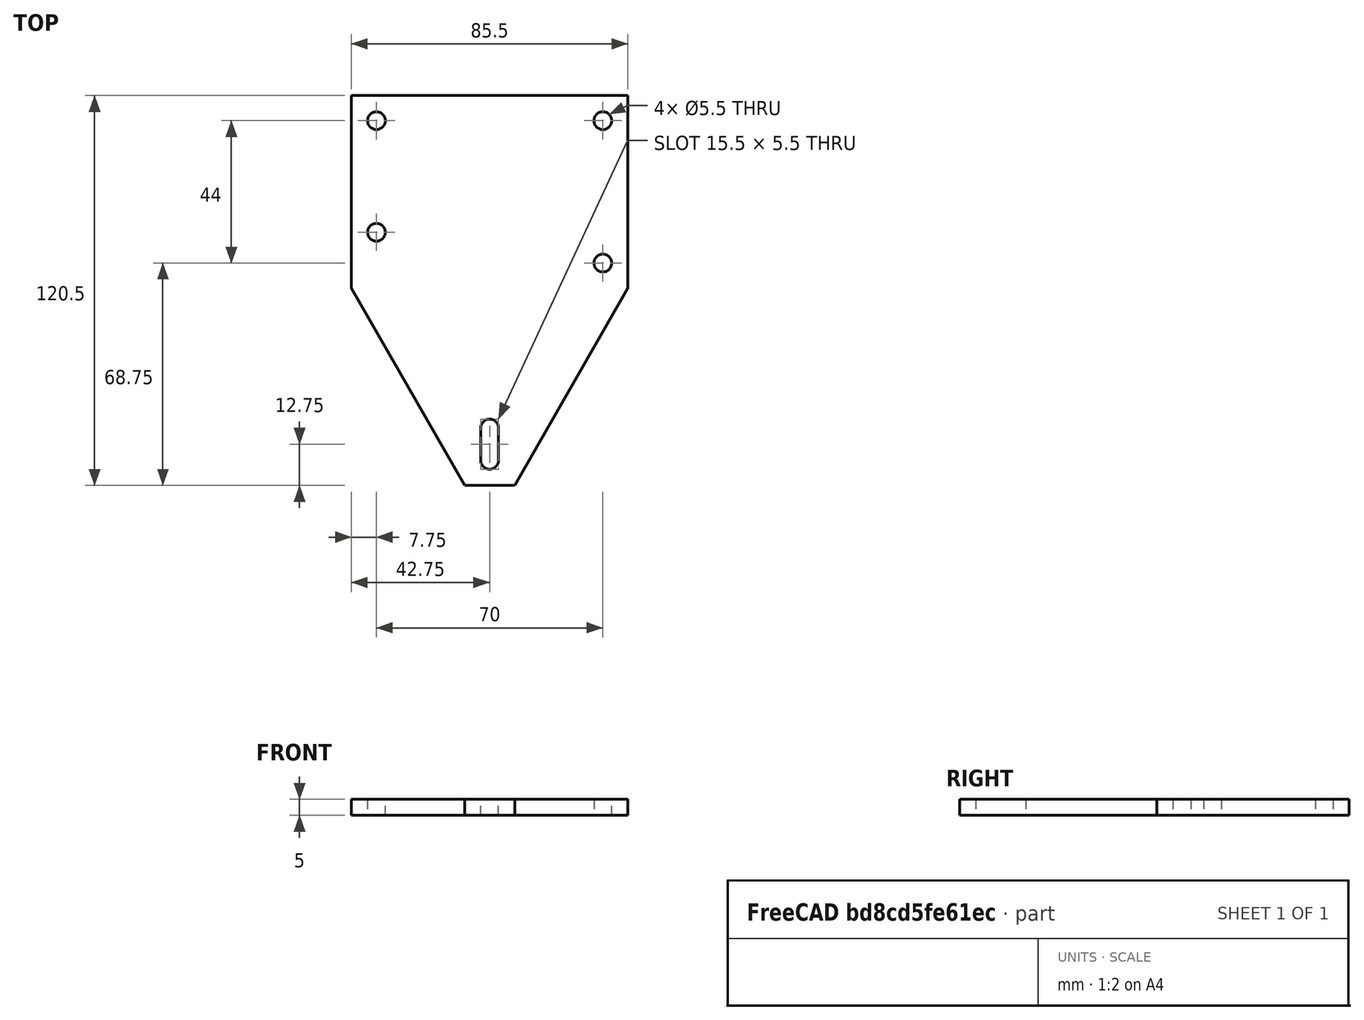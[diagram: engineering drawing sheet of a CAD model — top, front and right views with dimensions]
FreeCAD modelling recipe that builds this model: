
FCSTD DOCUMENT  (FreeCAD 0.19R)
Label: x-axis-top-carriage
License: All rights reserved
LicenseURL: http://en.wikipedia.org/wiki/All_rights_reserved
objects: Sketcher::SketchObject×1, PartDesign::Pad×1, PartDesign::Body×1
note: 4 computed .brp shape members not serialized (recipe doc carries the construction recipe); baked Part::Feature solids carry a one-line shape summary decoded from their .brp

FEATURE [Sketcher::SketchObject] Sketch
  FullyConstrained = true
  MapMode = 5
  Support = -> [XY_Plane]
  sketch-geometry (36):
    g0: LineSegment StartX=35 StartY=0 StartZ=0 EndX=50.5 EndY=0 EndZ=0
    g1: LineSegment StartX=50.5 StartY=0 StartZ=0 EndX=85.5 EndY=61 EndZ=0
    g2: LineSegment StartX=85.5 StartY=61 StartZ=0 EndX=85.5 EndY=120.5 EndZ=0
    g3: LineSegment StartX=0 StartY=120.5 StartZ=0 EndX=0 EndY=61 EndZ=0
    g4: LineSegment StartX=0 StartY=61 StartZ=0 EndX=35 EndY=0 EndZ=0
    g5: LineSegment StartX=42.75 StartY=120.5 StartZ=0 EndX=42.75 EndY=0 EndZ=0
    g6: LineSegment StartX=0 StartY=61 StartZ=0 EndX=85.5 EndY=61 EndZ=0
    g7: GeomPoint X=42.75 Y=61 Z=0
    g8: LineSegment StartX=40 StartY=17.75 StartZ=0 EndX=45.5 EndY=17.75 EndZ=0
    g9: LineSegment StartX=45.5 StartY=17.75 StartZ=0 EndX=45.5 EndY=7.75 EndZ=0
    g10: LineSegment StartX=45.5 StartY=7.75 StartZ=0 EndX=40 EndY=7.75 EndZ=0
    g11: LineSegment StartX=40 StartY=7.75 StartZ=0 EndX=40 EndY=17.75 EndZ=0
    g12: ArcOfCircle CenterX=42.75 CenterY=17.75 CenterZ=0 NormalX=0 NormalY=0 NormalZ=1 AngleXU=0 Radius=2.75 StartAngle=-2.7e-15 EndAngle=3.14159
    g13: ArcOfCircle CenterX=42.75 CenterY=7.75 CenterZ=0 NormalX=0 NormalY=0 NormalZ=1 AngleXU=0 Radius=2.75 StartAngle=3.14159 EndAngle=6.28319
    g14: GeomPoint X=42.75 Y=10.5 Z=0
    g15: GeomPoint X=42.75 Y=12.75 Z=0
    g16: LineSegment StartX=0 StartY=112.75 StartZ=0 EndX=85.5 EndY=112.75 EndZ=0
    g17: GeomPoint X=42.75 Y=112.75 Z=0
    g18: Circle CenterX=7.75 CenterY=112.75 CenterZ=0 NormalX=0 NormalY=0 NormalZ=1 AngleXU=0 Radius=2.75
    g19: Circle CenterX=77.75 CenterY=112.75 CenterZ=0 NormalX=0 NormalY=0 NormalZ=1 AngleXU=0 Radius=2.75
    g20: LineSegment StartX=7.75 StartY=120.5 StartZ=0 EndX=7.75 EndY=61 EndZ=0
    g21: GeomPoint X=7.75 Y=115.5 Z=0
    g22: GeomPoint X=5 Y=112.75 Z=0
    g23: GeomPoint X=42.75 Y=5 Z=0
    g24: LineSegment StartX=77.75 StartY=120.5 StartZ=0 EndX=77.75 EndY=61 EndZ=0
    g25: GeomPoint X=77.75 Y=115.5 Z=0
    g26: GeomPoint X=80.5 Y=112.75 Z=0
    g27: GeomPoint X=42.75 Y=62.75 Z=0
    g28: LineSegment StartX=0 StartY=68.75 StartZ=0 EndX=85.5 EndY=68.75 EndZ=0
    g29: GeomPoint X=42.75 Y=68.75 Z=0
    g30: LineSegment StartX=0 StartY=78.25 StartZ=0 EndX=85.5 EndY=78.25 EndZ=0
    g31: GeomPoint X=42.75 Y=78.25 Z=0
    g32: Circle CenterX=77.75 CenterY=68.75 CenterZ=0 NormalX=0 NormalY=0 NormalZ=1 AngleXU=0 Radius=2.75
    g33: Circle CenterX=7.75 CenterY=78.25 CenterZ=0 NormalX=0 NormalY=0 NormalZ=1 AngleXU=0 Radius=2.75
    g34: GeomPoint X=77.75 Y=66 Z=0
    g35: LineSegment StartX=0 StartY=120.5 StartZ=0 EndX=85.5 EndY=120.5 EndZ=0
  constraints (94):
    c: PointOnObject(g0,g-1)
    c: PointOnObject(g0,g-1)
    c: Coincident(g1,g0)
    c: Coincident(g2,g1)
    c: Vertical(g2)
    c: PointOnObject(g3,g-2)
    c: PointOnObject(g3,g-2)
    c: Coincident(g4,g3)
    c: Coincident(g4,g0)
    c: Vertical(g5)
    c: Symmetric(g0,g0,g5)
    c: Coincident(g6,g3)
    c: Coincident(g6,g1)
    c: Horizontal(g6)
    c: Symmetric(g1,g3,g7)
    c: Coincident(g8,g9)
    c: Coincident(g9,g10)
    c: Coincident(g10,g11)
    c: Coincident(g11,g8)
    c: Horizontal(g8)
    c: Horizontal(g10)
    c: Vertical(g9)
    c: Vertical(g11)
    c: PointOnObject(g12,g8)
    c: Coincident(g12,g8)
    c: Coincident(g12,g8)
    c: PointOnObject(g13,g10)
    c: Coincident(g13,g10)
    c: Coincident(g13,g9)
    c: PointOnObject(g13,g5)
    c: Diameter(g13) = 5.5
    c: PointOnObject(g14,g13)
    c: PointOnObject(g14,g5)
    c: DistanceX(g9,g0) = 5
    c: Symmetric(g12,g13,g15)
    c: PointOnObject(g16,g3)
    c: PointOnObject(g16,g2)
    c: Horizontal(g16)
    c: PointOnObject(g17,g5)
    c: PointOnObject(g17,g16)
    c: PointOnObject(g18,g16)
    c: PointOnObject(g19,g16)
    c: PointOnObject(g20,g6)
    c: Vertical(g20)
    c: PointOnObject(g18,g20)
    c: PointOnObject(g21,g18)
    c: PointOnObject(g21,g20)
    c: DistanceY(g21,g20) = 5
    c: PointOnObject(g22,g18)
    c: PointOnObject(g22,g16)
    c: DistanceX(g16,g22) = 5
    c: DistanceY(g15,g17) = 100
    c: PointOnObject(g23,g13)
    c: PointOnObject(g23,g5)
    c: DistanceY(g5,g23) = 5
    c: DistanceY(g9,g9) = 10
    c: Equal(g18,g19)
    c: Diameter(g18) = 5.5
    c: PointOnObject(g24,g6)
    c: Vertical(g24)
    c: PointOnObject(g19,g24)
    c: PointOnObject(g25,g19)
    c: PointOnObject(g26,g19)
    c: PointOnObject(g25,g24)
    c: PointOnObject(g26,g16)
    c: Symmetric(g17,g15,g27)
    c: PointOnObject(g28,g3)
    c: PointOnObject(g28,g2)
    c: Horizontal(g28)
    c: PointOnObject(g29,g28)
    c: PointOnObject(g29,g5)
    c: DistanceY(g27,g29) = 6
    c: PointOnObject(g30,g3)
    c: PointOnObject(g30,g2)
    c: Horizontal(g30)
    c: PointOnObject(g31,g30)
    c: PointOnObject(g31,g5)
    c: DistanceY(g27,g31) = 15.5
    c: DistanceX(g18,g19) = 70
    c: PointOnObject(g32,g28)
    c: PointOnObject(g33,g30)
    c: PointOnObject(g33,g20)
    c: PointOnObject(g32,g24)
    c: Equal(g33,g32)
    c: Equal(g32,g18)
    c: PointOnObject(g34,g32)
    c: PointOnObject(g34,g24)
    c: DistanceY(g24,g34) = 5
    c: Symmetric(g2,g3,g5)
    c: Symmetric(g24,g20,g5)
    c: Coincident(g35,g3)
    c: Coincident(g35,g2)
    c: Horizontal(g35)
    c: PointOnObject(g20,g35)
FEATURE [PartDesign::Pad] Pad
  Direction = (1,1,1)
  Length = 5
  Length2 = 100
  Profile = -> Sketch
  Type = 0
FEATURE [PartDesign::Body] Body
  Group = -> [Sketch,Pad]
  Origin = -> Origin
  Tip = -> Pad
